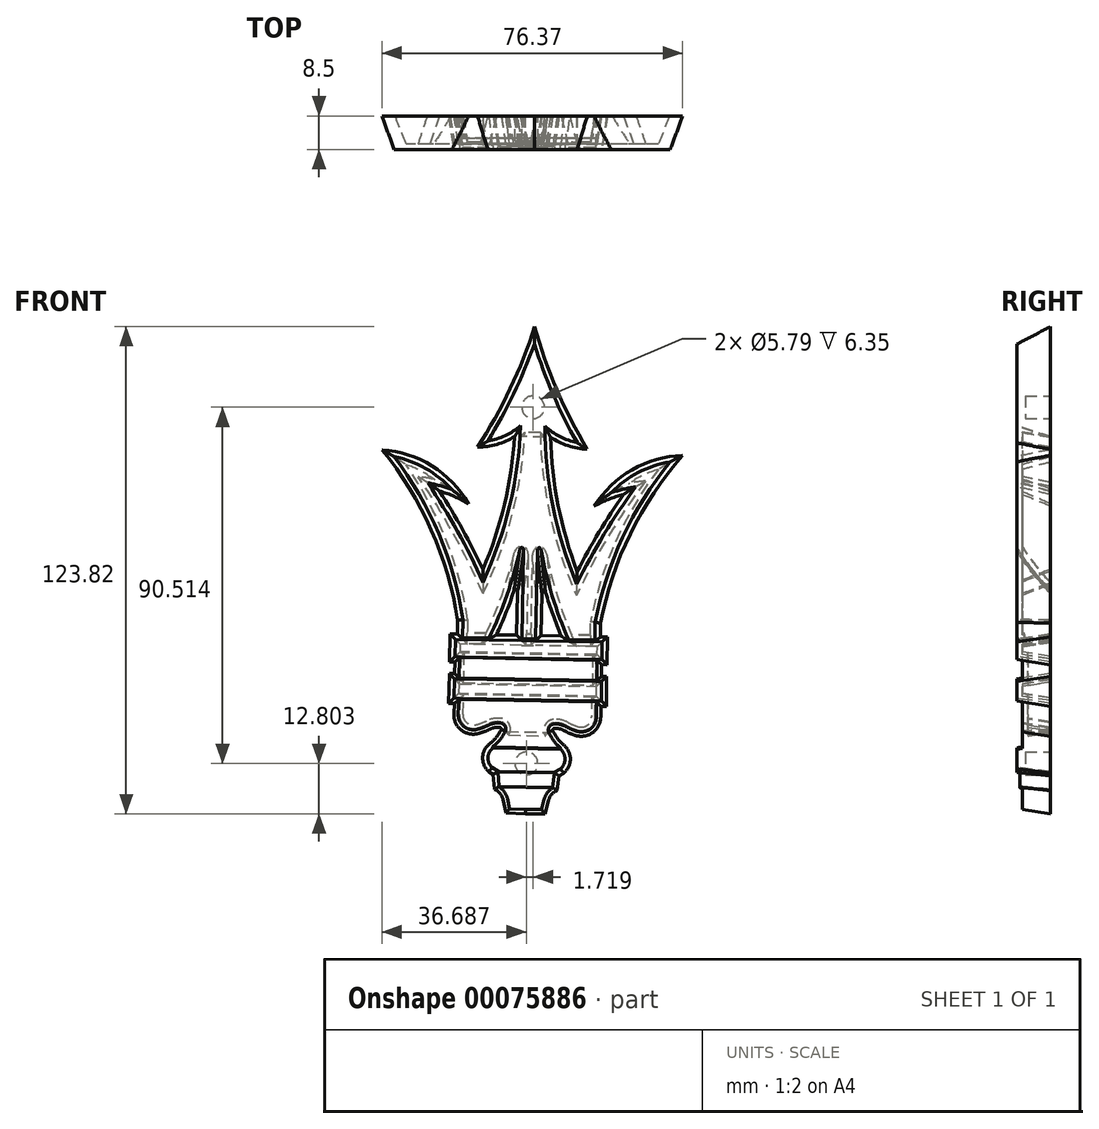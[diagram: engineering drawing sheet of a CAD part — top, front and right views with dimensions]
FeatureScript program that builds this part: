
annotation { "Feature Type Name" : "Feature", "Feature Type Description" : "" }
export const myFeature = defineFeature(function(context is Context, id is Id, definition is map)
    precondition{}
    {
        {
            var Q0;
            Q0=qCreatedBy(makeId("Front.planeOp"),FACE);
            var sketch = newSketch(context, id + "F0", { "sketchPlane" : qUnion([Q0])});
            skLineSegment(sketch, "E0", {"start": v(-26.98, -26.49) * mm, "end": v(-23.1, -26.49) * mm});
            skArc(sketch, "E1", {"start": v(-24.74, 91.51) * mm, "mid": v(-19.96, 78.7) * mm, "end": v(-13.84, 66.48) * mm});
            skArc(sketch, "E2", {"start": v(-22.03, 70.72) * mm, "mid": v(-18.24, 68.02) * mm, "end": v(-13.84, 66.48) * mm});
            skArc(sketch, "E3", {"start": v(-22.03, 70.72) * mm, "mid": v(-20, 50.24) * mm, "end": v(-14, 30.55) * mm});
            skArc(sketch, "E4", {"start": v(0.96, 55.26) * mm, "mid": v(-7.04, 43.22) * mm, "end": v(-14, 30.55) * mm});
            skArc(sketch, "E5", {"start": v(0.96, 55.26) * mm, "mid": v(-2.15, 54.66) * mm, "end": v(-5.19, 53.77) * mm});
            skArc(sketch, "E6", {"start": v(9.76, 61.58) * mm, "mid": v(1.64, 58.9) * mm, "end": v(-5.19, 53.77) * mm});
            skArc(sketch, "E7", {"start": v(9.76, 61.58) * mm, "mid": v(-2.3, 42.38) * mm, "end": v(-9.28, 20.8) * mm});
            skLineSegment(sketch, "E8", {"start": v(-9.28, 20.8) * mm, "end": v(-9.37, 15.85) * mm});
            skLineSegment(sketch, "E9", {"start": v(-9.37, 15.85) * mm, "end": v(-7.54, 15.82) * mm});
            skLineSegment(sketch, "E10", {"start": v(-7.54, 15.82) * mm, "end": v(-7.62, 11.41) * mm});
            skLineSegment(sketch, "E11", {"start": v(-7.62, 11.41) * mm, "end": v(-9.04, 11.44) * mm});
            skLineSegment(sketch, "E12", {"start": v(-9.04, 11.44) * mm, "end": v(-9.04, 5.77) * mm});
            skLineSegment(sketch, "E13", {"start": v(-9.04, 5.77) * mm, "end": v(-7.71, 5.77) * mm});
            skLineSegment(sketch, "E14", {"start": v(-7.71, 5.77) * mm, "end": v(-7.71, 0.87) * mm});
            skLineSegment(sketch, "E15", {"start": v(-7.71, 0.87) * mm, "end": v(-9.22, 0.87) * mm});
            skLineSegment(sketch, "E16", {"start": v(-9.22, 0.87) * mm, "end": v(-9.22, -3.16) * mm});
            skArc(sketch, "E17", {"start": v(-13.87, -6.61) * mm, "mid": v(-10.68, -6.06) * mm, "end": v(-9.22, -3.16) * mm});
            skArc(sketch, "E18", {"start": v(-16.67, -5.44) * mm, "mid": v(-15.3, -6.1) * mm, "end": v(-13.87, -6.61) * mm});
            skArc(sketch, "E19", {"start": v(-16.67, -5.44) * mm, "mid": v(-18.18, -4.88) * mm, "end": v(-19.78, -4.78) * mm});
            skArc(sketch, "E20", {"start": v(-19.78, -4.78) * mm, "mid": v(-21.12, -5.57) * mm, "end": v(-21.34, -7.1) * mm});
            skArc(sketch, "E21", {"start": v(-21.34, -7.1) * mm, "mid": v(-19.98, -9.44) * mm, "end": v(-18.11, -11.4) * mm});
            skArc(sketch, "E22", {"start": v(-18.11, -16.4) * mm, "mid": v(-16.94, -13.9) * mm, "end": v(-18.11, -11.4) * mm});
            skLineSegment(sketch, "E23", {"start": v(-18.11, -16.4) * mm, "end": v(-19.7, -17.36) * mm});
            skLineSegment(sketch, "E24", {"start": v(-19.7, -17.36) * mm, "end": v(-20.2, -21.02) * mm});
            skArc(sketch, "E25", {"start": v(-20.2, -21.02) * mm, "mid": v(-21.64, -22.32) * mm, "end": v(-22.48, -24.08) * mm});
            skLineSegment(sketch, "E26", {"start": v(-22.48, -24.08) * mm, "end": v(-23.1, -26.49) * mm});
            skLineSegment(sketch, "E27", {"start": v(-15.84, 15.97) * mm, "end": v(-24.42, 16.13) * mm});
            skLineSegment(sketch, "E28", {"start": v(-24.42, 16.13) * mm, "end": v(-23.86, 44.87) * mm});
            skArc(sketch, "E29", {"start": v(-23.86, 44.87) * mm, "mid": v(-20.95, 30.12) * mm, "end": v(-15.84, 15.97) * mm});
            skArc(sketch, "E30.MirrorCS", {"start": v(-24.74, 91.51) * mm, "mid": v(-30, 78.9) * mm, "end": v(-36.58, 66.91) * mm});
            skLineSegment(sketch, "E31.MirrorCS", {"start": v(-42.87, 21.44) * mm, "end": v(-42.97, 16.5) * mm});
            skLineSegment(sketch, "E32.MirrorCS", {"start": v(-42.97, 16.5) * mm, "end": v(-44.8, 16.53) * mm});
            skLineSegment(sketch, "E33.MirrorCS", {"start": v(-44.8, 16.53) * mm, "end": v(-44.89, 12.12) * mm});
            skLineSegment(sketch, "E34.MirrorCS", {"start": v(-44.89, 12.12) * mm, "end": v(-43.47, 12.1) * mm});
            skLineSegment(sketch, "E35.MirrorCS", {"start": v(-43.47, 12.1) * mm, "end": v(-43.68, 6.43) * mm});
            skLineSegment(sketch, "E36.MirrorCS", {"start": v(-43.68, 6.43) * mm, "end": v(-45.01, 6.48) * mm});
            skLineSegment(sketch, "E37.MirrorCS", {"start": v(-45.01, 6.48) * mm, "end": v(-45.2, 1.58) * mm});
            skLineSegment(sketch, "E38.MirrorCS", {"start": v(-45.2, 1.58) * mm, "end": v(-43.7, 1.52) * mm});
            skLineSegment(sketch, "E39.MirrorCS", {"start": v(-43.7, 1.52) * mm, "end": v(-43.85, -2.5) * mm});
            skArc(sketch, "E40.MirrorCS", {"start": v(-39.33, -6.13) * mm, "mid": v(-42.5, -5.45) * mm, "end": v(-43.85, -2.5) * mm});
            skArc(sketch, "E41.MirrorCS", {"start": v(-36.49, -5.06) * mm, "mid": v(-37.88, -5.67) * mm, "end": v(-39.33, -6.13) * mm});
            skArc(sketch, "E42.MirrorCS", {"start": v(-36.49, -5.06) * mm, "mid": v(-34.96, -4.56) * mm, "end": v(-33.35, -4.52) * mm});
            skArc(sketch, "E43.MirrorCS", {"start": v(-33.35, -4.52) * mm, "mid": v(-32.04, -5.36) * mm, "end": v(-31.88, -6.9) * mm});
            skArc(sketch, "E44.MirrorCS", {"start": v(-31.88, -6.9) * mm, "mid": v(-33.33, -9.18) * mm, "end": v(-35.27, -11.07) * mm});
            skArc(sketch, "E45.MirrorCS", {"start": v(-35.46, -16.06) * mm, "mid": v(-36.54, -13.52) * mm, "end": v(-35.27, -11.07) * mm});
            skLineSegment(sketch, "E46.MirrorCS", {"start": v(-35.46, -16.06) * mm, "end": v(-33.91, -17.1) * mm});
            skLineSegment(sketch, "E47.MirrorCS", {"start": v(-33.91, -17.1) * mm, "end": v(-33.56, -20.76) * mm});
            skArc(sketch, "E48.MirrorCS", {"start": v(-33.56, -20.76) * mm, "mid": v(-32.16, -22.12) * mm, "end": v(-31.39, -23.91) * mm});
            skLineSegment(sketch, "E49.MirrorCS", {"start": v(-31.39, -23.91) * mm, "end": v(-30.85, -26.34) * mm});
            skLineSegment(sketch, "E50.MirrorCS", {"start": v(-26.98, -26.49) * mm, "end": v(-30.85, -26.34) * mm});
            skLineSegment(sketch, "E51.MirrorCS", {"start": v(-36.5, 16.37) * mm, "end": v(-27.93, 16.2) * mm});
            skLineSegment(sketch, "E52.MirrorCS", {"start": v(-27.93, 16.2) * mm, "end": v(-27.4, 44.94) * mm});
            skArc(sketch, "E53.MirrorCS", {"start": v(-27.4, 44.94) * mm, "mid": v(-30.86, 30.3) * mm, "end": v(-36.5, 16.37) * mm});
            skArc(sketch, "E54.MirrorCS", {"start": v(-60.35, 62.9) * mm, "mid": v(-49.02, 43.27) * mm, "end": v(-42.87, 21.44) * mm});
            skArc(sketch, "E55.MirrorCS", {"start": v(-60.35, 62.9) * mm, "mid": v(-52.34, 59.93) * mm, "end": v(-45.71, 54.54) * mm});
            skArc(sketch, "E56.MirrorCS", {"start": v(-51.8, 56.26) * mm, "mid": v(-48.71, 55.55) * mm, "end": v(-45.71, 54.54) * mm});
            skArc(sketch, "E57.MirrorCS", {"start": v(-51.8, 56.26) * mm, "mid": v(-44.26, 43.93) * mm, "end": v(-37.8, 31) * mm});
            skArc(sketch, "E58.MirrorCS", {"start": v(-28.24, 70.83) * mm, "mid": v(-31.04, 50.45) * mm, "end": v(-37.8, 31) * mm});
            skArc(sketch, "E59.MirrorCS", {"start": v(-28.24, 70.83) * mm, "mid": v(-32.13, 68.28) * mm, "end": v(-36.58, 66.91) * mm});
            skSolve(sketch);
        }
        {
            var Q0;
            Q0=makeQuery(id+"F0.imprint","IMPRINT",FACE,{"disambiguationData":[TD([[makeQuery(id+"F0.imprint","IMPRINT",EDGE,{"derivedFrom":sQuery(id+"F0.wireOp",EDGE,"E0")}),1.0]])]});
            extrude(context, id + "F1", {"entities" : qUnion([Q0]), "oppositeDirection" : true, "depth" : 8.5 * mm, "hasDraft" : true, "draftAngle" : 9 * degree});
        }
        {
            var Q0;
            Q0=makeQuery(id+"F1.opExtrude","SWEPT_EDGE",EDGE,{"disambiguationData":[OSD([sQuery(id+"F0.wireOp",EDGE,"E52.MirrorCS"),sQuery(id+"F0.wireOp",EDGE,"E53.MirrorCS")])]});
            var Q1;
            Q1=makeQuery(id+"F1.opExtrude","SWEPT_EDGE",EDGE,{"disambiguationData":[OSD([sQuery(id+"F0.wireOp",EDGE,"E28"),sQuery(id+"F0.wireOp",EDGE,"E29")])]});
            fillet(context, id + "F2", {"entities" : qUnion([Q0, Q1]), "radius" : 0.5 * mm, "tangentPropagation" : true, "allowEdgeOverflow" : false});
        }
        {
            var Q0;
            Q0=makeQuery(id+"F1.opExtrude","CAP_FACE",FACE,{"disambiguationData":[OSD([sQuery(id+"F0.wireOp",EDGE,"E0"),sQuery(id+"F0.wireOp",EDGE,"E1"),sQuery(id+"F0.wireOp",EDGE,"E2"),sQuery(id+"F0.wireOp",EDGE,"E3"),sQuery(id+"F0.wireOp",EDGE,"E4"),sQuery(id+"F0.wireOp",EDGE,"E5"),sQuery(id+"F0.wireOp",EDGE,"E6"),sQuery(id+"F0.wireOp",EDGE,"E7"),sQuery(id+"F0.wireOp",EDGE,"E8"),sQuery(id+"F0.wireOp",EDGE,"E9"),sQuery(id+"F0.wireOp",EDGE,"E10"),sQuery(id+"F0.wireOp",EDGE,"E11"),sQuery(id+"F0.wireOp",EDGE,"E12"),sQuery(id+"F0.wireOp",EDGE,"E13"),sQuery(id+"F0.wireOp",EDGE,"E14"),sQuery(id+"F0.wireOp",EDGE,"E15"),sQuery(id+"F0.wireOp",EDGE,"E16"),sQuery(id+"F0.wireOp",EDGE,"E17"),sQuery(id+"F0.wireOp",EDGE,"E18"),sQuery(id+"F0.wireOp",EDGE,"E19"),sQuery(id+"F0.wireOp",EDGE,"E20"),sQuery(id+"F0.wireOp",EDGE,"E21"),sQuery(id+"F0.wireOp",EDGE,"E22"),sQuery(id+"F0.wireOp",EDGE,"E23"),sQuery(id+"F0.wireOp",EDGE,"E24"),sQuery(id+"F0.wireOp",EDGE,"E25"),sQuery(id+"F0.wireOp",EDGE,"E26"),sQuery(id+"F0.wireOp",EDGE,"E27"),sQuery(id+"F0.wireOp",EDGE,"E28"),sQuery(id+"F0.wireOp",EDGE,"E29"),sQuery(id+"F0.wireOp",EDGE,"E30.MirrorCS"),sQuery(id+"F0.wireOp",EDGE,"E31.MirrorCS"),sQuery(id+"F0.wireOp",EDGE,"E32.MirrorCS"),sQuery(id+"F0.wireOp",EDGE,"E33.MirrorCS"),sQuery(id+"F0.wireOp",EDGE,"E34.MirrorCS"),sQuery(id+"F0.wireOp",EDGE,"E35.MirrorCS"),sQuery(id+"F0.wireOp",EDGE,"E36.MirrorCS"),sQuery(id+"F0.wireOp",EDGE,"E37.MirrorCS"),sQuery(id+"F0.wireOp",EDGE,"E38.MirrorCS"),sQuery(id+"F0.wireOp",EDGE,"E39.MirrorCS"),sQuery(id+"F0.wireOp",EDGE,"E40.MirrorCS"),sQuery(id+"F0.wireOp",EDGE,"E41.MirrorCS"),sQuery(id+"F0.wireOp",EDGE,"E42.MirrorCS"),sQuery(id+"F0.wireOp",EDGE,"E43.MirrorCS"),sQuery(id+"F0.wireOp",EDGE,"E44.MirrorCS"),sQuery(id+"F0.wireOp",EDGE,"E45.MirrorCS"),sQuery(id+"F0.wireOp",EDGE,"E46.MirrorCS"),sQuery(id+"F0.wireOp",EDGE,"E47.MirrorCS"),sQuery(id+"F0.wireOp",EDGE,"E48.MirrorCS"),sQuery(id+"F0.wireOp",EDGE,"E49.MirrorCS"),sQuery(id+"F0.wireOp",EDGE,"E50.MirrorCS"),sQuery(id+"F0.wireOp",EDGE,"E51.MirrorCS"),sQuery(id+"F0.wireOp",EDGE,"E52.MirrorCS"),sQuery(id+"F0.wireOp",EDGE,"E53.MirrorCS"),sQuery(id+"F0.wireOp",EDGE,"E54.MirrorCS"),sQuery(id+"F0.wireOp",EDGE,"E55.MirrorCS"),sQuery(id+"F0.wireOp",EDGE,"E56.MirrorCS"),sQuery(id+"F0.wireOp",EDGE,"E57.MirrorCS"),sQuery(id+"F0.wireOp",EDGE,"E58.MirrorCS"),sQuery(id+"F0.wireOp",EDGE,"E59.MirrorCS")])],"isStart":true});
            var sketch = newSketch(context, id + "F3", { "sketchPlane" : qUnion([Q0])});
            skLineSegment(sketch, "E60", {"start": v(-43.47, 12.1) * mm, "end": v(-9.04, 11.44) * mm});
            skLineSegment(sketch, "E61", {"start": v(-9.04, 5.77) * mm, "end": v(-43.68, 6.43) * mm});
            skLineSegment(sketch, "E62", {"start": v(-43.7, 1.52) * mm, "end": v(-9.22, 0.87) * mm});
            skLineSegment(sketch, "E63", {"start": v(-9.22, 0.87) * mm, "end": v(-3.24, 0.87) * mm});
            skLineSegment(sketch, "E64", {"start": v(-3.24, 0.87) * mm, "end": v(-9.14, -11.57) * mm});
            skLineSegment(sketch, "E65", {"start": v(-9.14, -11.57) * mm, "end": v(-18.11, -11.4) * mm});
            skLineSegment(sketch, "E66", {"start": v(-18.11, -11.4) * mm, "end": v(-35.27, -11.07) * mm});
            skLineSegment(sketch, "E67", {"start": v(-35.27, -11.07) * mm, "end": v(-45.82, -10.87) * mm});
            skLineSegment(sketch, "E68", {"start": v(-45.82, -10.87) * mm, "end": v(-49.07, 1.73) * mm});
            skLineSegment(sketch, "E69", {"start": v(-49.07, 1.73) * mm, "end": v(-43.7, 1.52) * mm});
            skLineSegment(sketch, "E70", {"start": v(-33.56, -20.76) * mm, "end": v(-20.2, -21.02) * mm});
            skLineSegment(sketch, "E71", {"start": v(-20.2, -21.02) * mm, "end": v(-18, -22.48) * mm});
            skLineSegment(sketch, "E72", {"start": v(-18, -22.48) * mm, "end": v(-21.3, -29.33) * mm});
            skLineSegment(sketch, "E73", {"start": v(-21.3, -29.33) * mm, "end": v(-32.58, -28.86) * mm});
            skLineSegment(sketch, "E74", {"start": v(-32.58, -28.86) * mm, "end": v(-35.83, -22.18) * mm});
            skLineSegment(sketch, "E75", {"start": v(-35.83, -22.18) * mm, "end": v(-33.56, -20.76) * mm});
            skLineSegment(sketch, "E76", {"start": v(-43.47, 12.1) * mm, "end": v(-48.18, 12.19) * mm});
            skLineSegment(sketch, "E77", {"start": v(-48.18, 12.19) * mm, "end": v(-48.29, 6.6) * mm});
            skLineSegment(sketch, "E78", {"start": v(-48.29, 6.6) * mm, "end": v(-43.68, 6.43) * mm});
            skLineSegment(sketch, "E79", {"start": v(-9.04, 11.44) * mm, "end": v(-3.44, 11.34) * mm});
            skLineSegment(sketch, "E80", {"start": v(-3.44, 11.34) * mm, "end": v(-3.1, 5.77) * mm});
            skLineSegment(sketch, "E81", {"start": v(-3.1, 5.77) * mm, "end": v(-9.04, 5.77) * mm});
            skSolve(sketch);
        }
        {
            var Q0;
            {var subQ2=sQuery(id+"F3.wireOp",EDGE,"E77");Q0=makeQuery(id+"F3.imprint","IMPRINT",FACE,{"disambiguationData":[TD([[makeQuery(id+"F3.imprint","IMPRINT",EDGE,{"derivedFrom":subQ2}),1.0]])]});}
            var Q1;
            Q1=makeQuery(id+"F3.imprint","IMPRINT",FACE,{"disambiguationData":[TD([[makeQuery(id+"F3.imprint","IMPRINT",EDGE,{"derivedFrom":sQuery(id+"F3.wireOp",EDGE,"E60")}),-1.0]])]});
            var Q2;
            {var subQ0=sQuery(id+"F3.wireOp",EDGE,"E80");Q2=makeQuery(id+"F3.imprint","IMPRINT",FACE,{"disambiguationData":[TD([[makeQuery(id+"F3.imprint","IMPRINT",EDGE,{"derivedFrom":subQ0}),-1.0]])]});}
            var Q3;
            Q3=makeQuery(id+"F3.imprint","IMPRINT",FACE,{"disambiguationData":[TD([[makeQuery(id+"F3.imprint","IMPRINT",EDGE,{"derivedFrom":sQuery(id+"F3.wireOp",EDGE,"E67")}),-1.0]])]});
            var Q4;
            Q4=makeQuery(id+"F3.imprint","IMPRINT",FACE,{"disambiguationData":[TD([[makeQuery(id+"F3.imprint","IMPRINT",EDGE,{"derivedFrom":sQuery(id+"F3.wireOp",EDGE,"E62")}),-1.0]])]});
            var Q5;
            {var subQ3=sQuery(id+"F3.wireOp",EDGE,"E64");Q5=makeQuery(id+"F3.imprint","IMPRINT",FACE,{"disambiguationData":[TD([[makeQuery(id+"F3.imprint","IMPRINT",EDGE,{"derivedFrom":subQ3}),-1.0]])]});}
            var Q6;
            Q6=makeQuery(id+"F3.imprint","IMPRINT",FACE,{"disambiguationData":[TD([[makeQuery(id+"F3.imprint","IMPRINT",EDGE,{"derivedFrom":sQuery(id+"F3.wireOp",EDGE,"E70")}),-1.0]])]});
            var Q7;
            Q7=makeQuery(id+"F3.imprint","IMPRINT",FACE,{"disambiguationData":[TD([[makeQuery(id+"F3.imprint","IMPRINT",EDGE,{"derivedFrom":sQuery(id+"F3.wireOp",EDGE,"E71")}),-1.0]])]});
            extrude(context, id + "F4", {"entities" : qUnion([Q0, Q1, Q2, Q3, Q4, Q5, Q6, Q7]), "operationType" : NewBodyOperationType.REMOVE, "oppositeDirection" : true, "depth" : 1.5 * mm, "hasDraft" : true, "draftAngle" : 9 * degree, "draftPullDirection" : true});
        }
        {
            var Q0;
            {var subQ0=sQuery(id+"F0.wireOp",EDGE,"E48.MirrorCS");var subQ1=sQuery(id+"F0.wireOp",EDGE,"E24");var subQ2=sQuery(id+"F0.wireOp",EDGE,"E47.MirrorCS");var subQ3=sQuery(id+"F0.wireOp",EDGE,"E23");var subQ4=sQuery(id+"F0.wireOp",EDGE,"E46.MirrorCS");var subQ5=sQuery(id+"F0.wireOp",EDGE,"E25");var subQ6=sQuery(id+"F0.wireOp",EDGE,"E22");var subQ7=sQuery(id+"F0.wireOp",EDGE,"E21");var subQ8=sQuery(id+"F0.wireOp",EDGE,"E44.MirrorCS");var subQ9=sQuery(id+"F0.wireOp",EDGE,"E45.MirrorCS");Q0=makeQuery(id+"F4.boolean.opBoolean","SPLIT",FACE,{"disambiguationData":[TD([makeQuery(id+"F1.opExtrude","SWEPT_FACE",FACE,{"disambiguationData":[OSD([subQ7])]})])],"derivedFrom":makeQuery(id+"F1.opExtrude","CAP_FACE",FACE,{"disambiguationData":[OSD([sQuery(id+"F0.wireOp",EDGE,"E0"),sQuery(id+"F0.wireOp",EDGE,"E1"),sQuery(id+"F0.wireOp",EDGE,"E2"),sQuery(id+"F0.wireOp",EDGE,"E3"),sQuery(id+"F0.wireOp",EDGE,"E4"),sQuery(id+"F0.wireOp",EDGE,"E5"),sQuery(id+"F0.wireOp",EDGE,"E6"),sQuery(id+"F0.wireOp",EDGE,"E7"),sQuery(id+"F0.wireOp",EDGE,"E8"),sQuery(id+"F0.wireOp",EDGE,"E9"),sQuery(id+"F0.wireOp",EDGE,"E10"),sQuery(id+"F0.wireOp",EDGE,"E11"),sQuery(id+"F0.wireOp",EDGE,"E12"),sQuery(id+"F0.wireOp",EDGE,"E13"),sQuery(id+"F0.wireOp",EDGE,"E14"),sQuery(id+"F0.wireOp",EDGE,"E15"),sQuery(id+"F0.wireOp",EDGE,"E16"),sQuery(id+"F0.wireOp",EDGE,"E17"),sQuery(id+"F0.wireOp",EDGE,"E18"),sQuery(id+"F0.wireOp",EDGE,"E19"),sQuery(id+"F0.wireOp",EDGE,"E20"),subQ7,subQ6,subQ3,subQ1,subQ5,sQuery(id+"F0.wireOp",EDGE,"E26"),sQuery(id+"F0.wireOp",EDGE,"E27"),sQuery(id+"F0.wireOp",EDGE,"E28"),sQuery(id+"F0.wireOp",EDGE,"E29"),sQuery(id+"F0.wireOp",EDGE,"E30.MirrorCS"),sQuery(id+"F0.wireOp",EDGE,"E31.MirrorCS"),sQuery(id+"F0.wireOp",EDGE,"E32.MirrorCS"),sQuery(id+"F0.wireOp",EDGE,"E33.MirrorCS"),sQuery(id+"F0.wireOp",EDGE,"E34.MirrorCS"),sQuery(id+"F0.wireOp",EDGE,"E35.MirrorCS"),sQuery(id+"F0.wireOp",EDGE,"E36.MirrorCS"),sQuery(id+"F0.wireOp",EDGE,"E37.MirrorCS"),sQuery(id+"F0.wireOp",EDGE,"E38.MirrorCS"),sQuery(id+"F0.wireOp",EDGE,"E39.MirrorCS"),sQuery(id+"F0.wireOp",EDGE,"E40.MirrorCS"),sQuery(id+"F0.wireOp",EDGE,"E41.MirrorCS"),sQuery(id+"F0.wireOp",EDGE,"E42.MirrorCS"),sQuery(id+"F0.wireOp",EDGE,"E43.MirrorCS"),subQ8,subQ9,subQ4,subQ2,subQ0,sQuery(id+"F0.wireOp",EDGE,"E49.MirrorCS"),sQuery(id+"F0.wireOp",EDGE,"E50.MirrorCS"),sQuery(id+"F0.wireOp",EDGE,"E51.MirrorCS"),sQuery(id+"F0.wireOp",EDGE,"E52.MirrorCS"),sQuery(id+"F0.wireOp",EDGE,"E53.MirrorCS"),sQuery(id+"F0.wireOp",EDGE,"E54.MirrorCS"),sQuery(id+"F0.wireOp",EDGE,"E55.MirrorCS"),sQuery(id+"F0.wireOp",EDGE,"E56.MirrorCS"),sQuery(id+"F0.wireOp",EDGE,"E57.MirrorCS"),sQuery(id+"F0.wireOp",EDGE,"E58.MirrorCS"),sQuery(id+"F0.wireOp",EDGE,"E59.MirrorCS")])],"isStart":true})});}
            var sketch = newSketch(context, id + "F5", { "sketchPlane" : qUnion([Q0])});
            skLineSegment(sketch, "E82", {"start": v(-33.91, -17.1) * mm, "end": v(-19.7, -17.36) * mm});
            skLineSegment(sketch, "E83", {"start": v(-19.7, -17.36) * mm, "end": v(-16.05, -17.43) * mm});
            skLineSegment(sketch, "E84", {"start": v(-16.05, -17.43) * mm, "end": v(-18.1, -23.56) * mm});
            skLineSegment(sketch, "E85", {"start": v(-18.1, -23.56) * mm, "end": v(-35.42, -23.56) * mm});
            skLineSegment(sketch, "E86", {"start": v(-35.42, -23.56) * mm, "end": v(-36.7, -17.04) * mm});
            skLineSegment(sketch, "E87", {"start": v(-36.7, -17.04) * mm, "end": v(-33.91, -17.1) * mm});
            skSolve(sketch);
        }
        {
            var Q0;
            Q0 = qSketchRegion(id + "F5", true);
            extrude(context, id + "F6", {"entities" : qUnion([Q0]), "operationType" : NewBodyOperationType.REMOVE, "oppositeDirection" : true, "depth" : 0.75 * mm, "hasDraft" : true, "draftAngle" : 9 * degree, "draftPullDirection" : true});
        }
        {
            var Q0;
            {var subQ0=sQuery(id+"F0.wireOp",EDGE,"E53.MirrorCS");var subQ1=sQuery(id+"F0.wireOp",EDGE,"E4");var subQ2=sQuery(id+"F0.wireOp",EDGE,"E31.MirrorCS");var subQ3=sQuery(id+"F0.wireOp",EDGE,"E33.MirrorCS");var subQ4=sQuery(id+"F0.wireOp",EDGE,"E30.MirrorCS");var subQ5=sQuery(id+"F0.wireOp",EDGE,"E32.MirrorCS");var subQ6=sQuery(id+"F0.wireOp",EDGE,"E51.MirrorCS");var subQ7=sQuery(id+"F0.wireOp",EDGE,"E2");var subQ8=sQuery(id+"F0.wireOp",EDGE,"E59.MirrorCS");var subQ9=sQuery(id+"F0.wireOp",EDGE,"E34.MirrorCS");var subQ10=sQuery(id+"F0.wireOp",EDGE,"E27");var subQ11=sQuery(id+"F0.wireOp",EDGE,"E11");var subQ12=sQuery(id+"F0.wireOp",EDGE,"E58.MirrorCS");var subQ13=sQuery(id+"F0.wireOp",EDGE,"E3");var subQ14=sQuery(id+"F0.wireOp",EDGE,"E52.MirrorCS");var subQ15=sQuery(id+"F0.wireOp",EDGE,"E10");var subQ16=sQuery(id+"F0.wireOp",EDGE,"E28");var subQ17=sQuery(id+"F0.wireOp",EDGE,"E1");var subQ18=sQuery(id+"F0.wireOp",EDGE,"E8");var subQ19=sQuery(id+"F0.wireOp",EDGE,"E57.MirrorCS");var subQ20=sQuery(id+"F0.wireOp",EDGE,"E29");var subQ21=sQuery(id+"F0.wireOp",EDGE,"E5");var subQ22=sQuery(id+"F0.wireOp",EDGE,"E6");var subQ23=sQuery(id+"F0.wireOp",EDGE,"E55.MirrorCS");var subQ24=sQuery(id+"F0.wireOp",EDGE,"E7");var subQ25=sQuery(id+"F0.wireOp",EDGE,"E54.MirrorCS");var subQ26=sQuery(id+"F0.wireOp",EDGE,"E56.MirrorCS");var subQ27=sQuery(id+"F0.wireOp",EDGE,"E9");Q0=makeQuery(id+"F4.boolean.opBoolean","SPLIT",FACE,{"disambiguationData":[TD([makeQuery(id+"F1.opExtrude","SWEPT_FACE",FACE,{"disambiguationData":[OSD([subQ17])]})])],"derivedFrom":makeQuery(id+"F1.opExtrude","CAP_FACE",FACE,{"disambiguationData":[OSD([sQuery(id+"F0.wireOp",EDGE,"E0"),subQ17,subQ7,subQ13,subQ1,subQ21,subQ22,subQ24,subQ18,subQ27,subQ15,subQ11,sQuery(id+"F0.wireOp",EDGE,"E12"),sQuery(id+"F0.wireOp",EDGE,"E13"),sQuery(id+"F0.wireOp",EDGE,"E14"),sQuery(id+"F0.wireOp",EDGE,"E15"),sQuery(id+"F0.wireOp",EDGE,"E16"),sQuery(id+"F0.wireOp",EDGE,"E17"),sQuery(id+"F0.wireOp",EDGE,"E18"),sQuery(id+"F0.wireOp",EDGE,"E19"),sQuery(id+"F0.wireOp",EDGE,"E20"),sQuery(id+"F0.wireOp",EDGE,"E21"),sQuery(id+"F0.wireOp",EDGE,"E22"),sQuery(id+"F0.wireOp",EDGE,"E23"),sQuery(id+"F0.wireOp",EDGE,"E24"),sQuery(id+"F0.wireOp",EDGE,"E25"),sQuery(id+"F0.wireOp",EDGE,"E26"),subQ10,subQ16,subQ20,subQ4,subQ2,subQ5,subQ3,subQ9,sQuery(id+"F0.wireOp",EDGE,"E35.MirrorCS"),sQuery(id+"F0.wireOp",EDGE,"E36.MirrorCS"),sQuery(id+"F0.wireOp",EDGE,"E37.MirrorCS"),sQuery(id+"F0.wireOp",EDGE,"E38.MirrorCS"),sQuery(id+"F0.wireOp",EDGE,"E39.MirrorCS"),sQuery(id+"F0.wireOp",EDGE,"E40.MirrorCS"),sQuery(id+"F0.wireOp",EDGE,"E41.MirrorCS"),sQuery(id+"F0.wireOp",EDGE,"E42.MirrorCS"),sQuery(id+"F0.wireOp",EDGE,"E43.MirrorCS"),sQuery(id+"F0.wireOp",EDGE,"E44.MirrorCS"),sQuery(id+"F0.wireOp",EDGE,"E45.MirrorCS"),sQuery(id+"F0.wireOp",EDGE,"E46.MirrorCS"),sQuery(id+"F0.wireOp",EDGE,"E47.MirrorCS"),sQuery(id+"F0.wireOp",EDGE,"E48.MirrorCS"),sQuery(id+"F0.wireOp",EDGE,"E49.MirrorCS"),sQuery(id+"F0.wireOp",EDGE,"E50.MirrorCS"),subQ6,subQ14,subQ0,subQ25,subQ23,subQ26,subQ19,subQ12,subQ8])],"isStart":true})});}
            var sketch = newSketch(context, id + "F7", { "sketchPlane" : qUnion([Q0])});
            skLineSegment(sketch, "E88", {"start": v(-42.97, 16.5) * mm, "end": v(-36.5, 16.37) * mm});
            skLineSegment(sketch, "E89", {"start": v(-36.5, 16.37) * mm, "end": v(-27.93, 16.2) * mm});
            skLineSegment(sketch, "E90", {"start": v(-27.93, 16.2) * mm, "end": v(-24.42, 16.13) * mm});
            skLineSegment(sketch, "E91", {"start": v(-24.42, 16.13) * mm, "end": v(-15.84, 15.97) * mm});
            skLineSegment(sketch, "E92", {"start": v(-15.84, 15.97) * mm, "end": v(-9.37, 15.85) * mm});
            skLineSegment(sketch, "E93", {"start": v(-9.37, 15.85) * mm, "end": v(-7.54, 15.82) * mm});
            skLineSegment(sketch, "E94", {"start": v(-42.97, 16.5) * mm, "end": v(-44.8, 16.53) * mm});
            skLineSegment(sketch, "E95.0", {"start": v(-42.96, 17) * mm, "end": v(-44.8, 17.03) * mm});
            skLineSegment(sketch, "E95.1", {"start": v(-42.96, 17) * mm, "end": v(-36.5, 16.87) * mm});
            skLineSegment(sketch, "E95.2", {"start": v(-36.5, 16.87) * mm, "end": v(-27.92, 16.7) * mm});
            skLineSegment(sketch, "E95.3", {"start": v(-9.36, 16.35) * mm, "end": v(-7.53, 16.32) * mm});
            skLineSegment(sketch, "E95.4", {"start": v(-15.83, 16.47) * mm, "end": v(-9.36, 16.35) * mm});
            skLineSegment(sketch, "E95.5", {"start": v(-24.4, 16.63) * mm, "end": v(-15.83, 16.47) * mm});
            skLineSegment(sketch, "E95.6", {"start": v(-27.92, 16.7) * mm, "end": v(-24.4, 16.63) * mm});
            skLineSegment(sketch, "E96", {"start": v(-44.8, 16.53) * mm, "end": v(-44.8, 17.03) * mm});
            skLineSegment(sketch, "E97", {"start": v(-7.54, 15.82) * mm, "end": v(-7.53, 16.32) * mm});
            skSolve(sketch);
        }
        {
            var Q0;
            {var subQ0=sQuery(id+"F7.wireOp",EDGE,"E94");Q0=makeQuery(id+"F7.imprint","IMPRINT",FACE,{"disambiguationData":[TD([[makeQuery(id+"F7.imprint","IMPRINT",EDGE,{"derivedFrom":subQ0}),-1.0]])]});}
            var Q1;
            {var subQ0=sQuery(id+"F7.wireOp",EDGE,"E88");Q1=makeQuery(id+"F7.imprint","IMPRINT",FACE,{"disambiguationData":[TD([[makeQuery(id+"F7.imprint","IMPRINT",EDGE,{"derivedFrom":subQ0}),1.0]])]});}
            var Q2;
            {var subQ0=sQuery(id+"F7.wireOp",EDGE,"E89");Q2=makeQuery(id+"F7.imprint","IMPRINT",FACE,{"disambiguationData":[TD([[makeQuery(id+"F7.imprint","IMPRINT",EDGE,{"derivedFrom":subQ0}),1.0]])]});}
            var Q3;
            {var subQ1=sQuery(id+"F7.wireOp",EDGE,"E90");Q3=makeQuery(id+"F7.imprint","IMPRINT",FACE,{"disambiguationData":[TD([[makeQuery(id+"F7.imprint","IMPRINT",EDGE,{"derivedFrom":subQ1}),1.0]])]});}
            var Q4;
            {var subQ0=sQuery(id+"F7.wireOp",EDGE,"E91");Q4=makeQuery(id+"F7.imprint","IMPRINT",FACE,{"disambiguationData":[TD([[makeQuery(id+"F7.imprint","IMPRINT",EDGE,{"derivedFrom":subQ0}),-1.0]])]});}
            var Q5;
            {var subQ4=sQuery(id+"F7.wireOp",EDGE,"E92");Q5=makeQuery(id+"F7.imprint","IMPRINT",FACE,{"disambiguationData":[TD([[makeQuery(id+"F7.imprint","IMPRINT",EDGE,{"derivedFrom":subQ4}),1.0]])]});}
            var Q6;
            {var subQ0=sQuery(id+"F7.wireOp",EDGE,"E93");Q6=makeQuery(id+"F7.imprint","IMPRINT",FACE,{"disambiguationData":[TD([[makeQuery(id+"F7.imprint","IMPRINT",EDGE,{"derivedFrom":subQ0}),1.0]])]});}
            extrude(context, id + "F8", {"entities" : qUnion([Q0, Q1, Q2, Q3, Q4, Q5, Q6]), "operationType" : NewBodyOperationType.REMOVE, "oppositeDirection" : true, "depth" : 0.5 * mm, "hasDraft" : true, "draftAngle" : 9 * degree, "draftPullDirection" : true});
        }
        {
            var Q0;
            Q0=makeQuery(id+"F1.opExtrude","CAP_FACE",FACE,{"disambiguationData":[OSD([sQuery(id+"F0.wireOp",EDGE,"E0"),sQuery(id+"F0.wireOp",EDGE,"E1"),sQuery(id+"F0.wireOp",EDGE,"E2"),sQuery(id+"F0.wireOp",EDGE,"E3"),sQuery(id+"F0.wireOp",EDGE,"E4"),sQuery(id+"F0.wireOp",EDGE,"E5"),sQuery(id+"F0.wireOp",EDGE,"E6"),sQuery(id+"F0.wireOp",EDGE,"E7"),sQuery(id+"F0.wireOp",EDGE,"E8"),sQuery(id+"F0.wireOp",EDGE,"E9"),sQuery(id+"F0.wireOp",EDGE,"E10"),sQuery(id+"F0.wireOp",EDGE,"E11"),sQuery(id+"F0.wireOp",EDGE,"E12"),sQuery(id+"F0.wireOp",EDGE,"E13"),sQuery(id+"F0.wireOp",EDGE,"E14"),sQuery(id+"F0.wireOp",EDGE,"E15"),sQuery(id+"F0.wireOp",EDGE,"E16"),sQuery(id+"F0.wireOp",EDGE,"E17"),sQuery(id+"F0.wireOp",EDGE,"E18"),sQuery(id+"F0.wireOp",EDGE,"E19"),sQuery(id+"F0.wireOp",EDGE,"E20"),sQuery(id+"F0.wireOp",EDGE,"E21"),sQuery(id+"F0.wireOp",EDGE,"E22"),sQuery(id+"F0.wireOp",EDGE,"E23"),sQuery(id+"F0.wireOp",EDGE,"E24"),sQuery(id+"F0.wireOp",EDGE,"E25"),sQuery(id+"F0.wireOp",EDGE,"E26"),sQuery(id+"F0.wireOp",EDGE,"E27"),sQuery(id+"F0.wireOp",EDGE,"E28"),sQuery(id+"F0.wireOp",EDGE,"E29"),sQuery(id+"F0.wireOp",EDGE,"E30.MirrorCS"),sQuery(id+"F0.wireOp",EDGE,"E31.MirrorCS"),sQuery(id+"F0.wireOp",EDGE,"E32.MirrorCS"),sQuery(id+"F0.wireOp",EDGE,"E33.MirrorCS"),sQuery(id+"F0.wireOp",EDGE,"E34.MirrorCS"),sQuery(id+"F0.wireOp",EDGE,"E35.MirrorCS"),sQuery(id+"F0.wireOp",EDGE,"E36.MirrorCS"),sQuery(id+"F0.wireOp",EDGE,"E37.MirrorCS"),sQuery(id+"F0.wireOp",EDGE,"E38.MirrorCS"),sQuery(id+"F0.wireOp",EDGE,"E39.MirrorCS"),sQuery(id+"F0.wireOp",EDGE,"E40.MirrorCS"),sQuery(id+"F0.wireOp",EDGE,"E41.MirrorCS"),sQuery(id+"F0.wireOp",EDGE,"E42.MirrorCS"),sQuery(id+"F0.wireOp",EDGE,"E43.MirrorCS"),sQuery(id+"F0.wireOp",EDGE,"E44.MirrorCS"),sQuery(id+"F0.wireOp",EDGE,"E45.MirrorCS"),sQuery(id+"F0.wireOp",EDGE,"E46.MirrorCS"),sQuery(id+"F0.wireOp",EDGE,"E47.MirrorCS"),sQuery(id+"F0.wireOp",EDGE,"E48.MirrorCS"),sQuery(id+"F0.wireOp",EDGE,"E49.MirrorCS"),sQuery(id+"F0.wireOp",EDGE,"E50.MirrorCS"),sQuery(id+"F0.wireOp",EDGE,"E51.MirrorCS"),sQuery(id+"F0.wireOp",EDGE,"E52.MirrorCS"),sQuery(id+"F0.wireOp",EDGE,"E53.MirrorCS"),sQuery(id+"F0.wireOp",EDGE,"E54.MirrorCS"),sQuery(id+"F0.wireOp",EDGE,"E55.MirrorCS"),sQuery(id+"F0.wireOp",EDGE,"E56.MirrorCS"),sQuery(id+"F0.wireOp",EDGE,"E57.MirrorCS"),sQuery(id+"F0.wireOp",EDGE,"E58.MirrorCS"),sQuery(id+"F0.wireOp",EDGE,"E59.MirrorCS")])],"isStart":false});
            shell(context, id + "F9", {"entities" : qUnion([Q0]), "thickness" : 1.4 * mm});
        }
        {
            var Q0;
            {var subQ0=sQuery(id+"F0.wireOp",EDGE,"E59.MirrorCS");var subQ1=sQuery(id+"F0.wireOp",EDGE,"E58.MirrorCS");var subQ2=sQuery(id+"F0.wireOp",EDGE,"E57.MirrorCS");var subQ3=sQuery(id+"F0.wireOp",EDGE,"E56.MirrorCS");var subQ4=sQuery(id+"F0.wireOp",EDGE,"E55.MirrorCS");var subQ5=sQuery(id+"F0.wireOp",EDGE,"E54.MirrorCS");var subQ6=sQuery(id+"F0.wireOp",EDGE,"E53.MirrorCS");var subQ7=sQuery(id+"F0.wireOp",EDGE,"E52.MirrorCS");var subQ8=sQuery(id+"F0.wireOp",EDGE,"E51.MirrorCS");var subQ9=sQuery(id+"F0.wireOp",EDGE,"E50.MirrorCS");var subQ10=sQuery(id+"F0.wireOp",EDGE,"E49.MirrorCS");var subQ11=sQuery(id+"F0.wireOp",EDGE,"E48.MirrorCS");var subQ12=sQuery(id+"F0.wireOp",EDGE,"E47.MirrorCS");var subQ13=sQuery(id+"F0.wireOp",EDGE,"E46.MirrorCS");var subQ14=sQuery(id+"F0.wireOp",EDGE,"E45.MirrorCS");var subQ15=sQuery(id+"F0.wireOp",EDGE,"E44.MirrorCS");var subQ16=sQuery(id+"F0.wireOp",EDGE,"E43.MirrorCS");var subQ17=sQuery(id+"F0.wireOp",EDGE,"E42.MirrorCS");var subQ18=sQuery(id+"F0.wireOp",EDGE,"E41.MirrorCS");var subQ19=sQuery(id+"F0.wireOp",EDGE,"E40.MirrorCS");var subQ20=sQuery(id+"F0.wireOp",EDGE,"E39.MirrorCS");var subQ21=sQuery(id+"F0.wireOp",EDGE,"E38.MirrorCS");var subQ22=sQuery(id+"F0.wireOp",EDGE,"E37.MirrorCS");var subQ23=sQuery(id+"F0.wireOp",EDGE,"E36.MirrorCS");var subQ24=sQuery(id+"F0.wireOp",EDGE,"E35.MirrorCS");var subQ25=sQuery(id+"F0.wireOp",EDGE,"E34.MirrorCS");var subQ26=sQuery(id+"F0.wireOp",EDGE,"E33.MirrorCS");var subQ27=sQuery(id+"F0.wireOp",EDGE,"E32.MirrorCS");var subQ28=sQuery(id+"F0.wireOp",EDGE,"E31.MirrorCS");var subQ29=sQuery(id+"F0.wireOp",EDGE,"E30.MirrorCS");var subQ30=sQuery(id+"F0.wireOp",EDGE,"E29");var subQ31=sQuery(id+"F0.wireOp",EDGE,"E28");var subQ32=sQuery(id+"F0.wireOp",EDGE,"E27");var subQ33=sQuery(id+"F0.wireOp",EDGE,"E26");var subQ34=sQuery(id+"F0.wireOp",EDGE,"E25");var subQ35=sQuery(id+"F0.wireOp",EDGE,"E24");var subQ36=sQuery(id+"F0.wireOp",EDGE,"E23");var subQ37=sQuery(id+"F0.wireOp",EDGE,"E22");var subQ38=sQuery(id+"F0.wireOp",EDGE,"E21");var subQ39=sQuery(id+"F0.wireOp",EDGE,"E20");var subQ40=sQuery(id+"F0.wireOp",EDGE,"E19");var subQ41=sQuery(id+"F0.wireOp",EDGE,"E18");var subQ42=sQuery(id+"F0.wireOp",EDGE,"E17");var subQ43=sQuery(id+"F0.wireOp",EDGE,"E16");var subQ44=sQuery(id+"F0.wireOp",EDGE,"E15");var subQ45=sQuery(id+"F0.wireOp",EDGE,"E14");var subQ46=sQuery(id+"F0.wireOp",EDGE,"E13");var subQ47=sQuery(id+"F0.wireOp",EDGE,"E12");var subQ48=sQuery(id+"F0.wireOp",EDGE,"E11");var subQ49=sQuery(id+"F0.wireOp",EDGE,"E10");var subQ50=sQuery(id+"F0.wireOp",EDGE,"E9");var subQ51=sQuery(id+"F0.wireOp",EDGE,"E8");var subQ52=sQuery(id+"F0.wireOp",EDGE,"E7");var subQ53=sQuery(id+"F0.wireOp",EDGE,"E6");var subQ54=sQuery(id+"F0.wireOp",EDGE,"E5");var subQ55=sQuery(id+"F0.wireOp",EDGE,"E4");var subQ56=sQuery(id+"F0.wireOp",EDGE,"E3");var subQ57=sQuery(id+"F0.wireOp",EDGE,"E2");var subQ58=sQuery(id+"F0.wireOp",EDGE,"E1");var subQ59=sQuery(id+"F0.wireOp",EDGE,"E0");Q0=makeQuery(id+"F9.opShell","OFFSET_FACE",FACE,{"disambiguationData":[OSD([subQ59,subQ58,subQ57,subQ56,subQ55,subQ54,subQ53,subQ52,subQ51,subQ50,subQ49,subQ48,subQ47,subQ46,subQ45,subQ44,subQ43,subQ42,subQ41,subQ40,subQ39,subQ38,subQ37,subQ36,subQ35,subQ34,subQ33,subQ32,subQ31,subQ30,subQ29,subQ28,subQ27,subQ26,subQ25,subQ24,subQ23,subQ22,subQ21,subQ20,subQ19,subQ18,subQ17,subQ16,subQ15,subQ14,subQ13,subQ12,subQ11,subQ10,subQ9,subQ8,subQ7,subQ6,subQ5,subQ4,subQ3,subQ2,subQ1,subQ0]),TDD([makeQuery(id+"F1.opExtrude","CAP_FACE",FACE,{"disambiguationData":[OSD([subQ59,subQ58,subQ57,subQ56,subQ55,subQ54,subQ53,subQ52,subQ51,subQ50,subQ49,subQ48,subQ47,subQ46,subQ45,subQ44,subQ43,subQ42,subQ41,subQ40,subQ39,subQ38,subQ37,subQ36,subQ35,subQ34,subQ33,subQ32,subQ31,subQ30,subQ29,subQ28,subQ27,subQ26,subQ25,subQ24,subQ23,subQ22,subQ21,subQ20,subQ19,subQ18,subQ17,subQ16,subQ15,subQ14,subQ13,subQ12,subQ11,subQ10,subQ9,subQ8,subQ7,subQ6,subQ5,subQ4,subQ3,subQ2,subQ1,subQ0])],"isStart":false})]),OD(1.0)]});}
            var sketch = newSketch(context, id + "F10", { "sketchPlane" : qUnion([Q0])});
            skLineSegment(sketch, "E98", {"start": v(21.41, -7.13) * mm, "end": v(31.81, -6.93) * mm});
            skLineSegment(sketch, "E99", {"start": v(20.65, 67.89) * mm, "end": v(29.73, 68.06) * mm});
            skSolve(sketch);
        }
        {
            var Q0;
            {var subQ3=sQuery(id+"F0.wireOp",EDGE,"E1");Q0=makeQuery(id+"F10.imprint","IMPRINT",FACE,{"disambiguationData":[TD([[makeQuery(id+"F10.imprint","IMPRINT",EDGE,{"derivedFrom":makeQuery(id+"F9.opShell","OFFSET_EDGE",EDGE,{"disambiguationData":[OSD([subQ3]),TDD([makeQuery(id+"F1.opExtrude","CAP_EDGE",EDGE,{"disambiguationData":[OSD([subQ3])],"isStart":false})])]})}),1.0]])]});}
            var Q1;
            Q1=makeQuery(id+"F10.imprint","IMPRINT",FACE,{"disambiguationData":[TD([[makeQuery(id+"F10.imprint","IMPRINT",EDGE,{"derivedFrom":sQuery(id+"F10.wireOp",EDGE,"E98")}),-1.0]])]});
            extrude(context, id + "F11", {"entities" : qUnion([Q0, Q1]), "operationType" : NewBodyOperationType.ADD, "endBound" : BoundingType.UP_TO_NEXT, "oppositeDirection" : true, "depth" : 8 * mm, "hasDraft" : true, "draftAngle" : 9 * degree, "draftPullDirection" : true});
        }
        {
            var Q0;
            {var subQ0=sQuery(id+"F0.wireOp",EDGE,"E59.MirrorCS");var subQ1=sQuery(id+"F0.wireOp",EDGE,"E58.MirrorCS");var subQ2=sQuery(id+"F0.wireOp",EDGE,"E30.MirrorCS");var subQ3=sQuery(id+"F0.wireOp",EDGE,"E3");var subQ4=sQuery(id+"F0.wireOp",EDGE,"E2");var subQ5=sQuery(id+"F0.wireOp",EDGE,"E1");var subQ6=sQuery(id+"F0.wireOp",EDGE,"E50.MirrorCS");var subQ7=sQuery(id+"F0.wireOp",EDGE,"E49.MirrorCS");var subQ8=sQuery(id+"F0.wireOp",EDGE,"E48.MirrorCS");var subQ9=sQuery(id+"F0.wireOp",EDGE,"E47.MirrorCS");var subQ10=sQuery(id+"F0.wireOp",EDGE,"E46.MirrorCS");var subQ11=sQuery(id+"F0.wireOp",EDGE,"E45.MirrorCS");var subQ12=sQuery(id+"F0.wireOp",EDGE,"E44.MirrorCS");var subQ13=sQuery(id+"F0.wireOp",EDGE,"E26");var subQ14=sQuery(id+"F0.wireOp",EDGE,"E25");var subQ15=sQuery(id+"F0.wireOp",EDGE,"E24");var subQ16=sQuery(id+"F0.wireOp",EDGE,"E23");var subQ17=sQuery(id+"F0.wireOp",EDGE,"E22");var subQ18=sQuery(id+"F0.wireOp",EDGE,"E21");var subQ19=sQuery(id+"F0.wireOp",EDGE,"E0");var subQ20=sQuery(id+"F0.wireOp",EDGE,"E57.MirrorCS");var subQ21=sQuery(id+"F0.wireOp",EDGE,"E56.MirrorCS");var subQ22=sQuery(id+"F0.wireOp",EDGE,"E55.MirrorCS");var subQ23=sQuery(id+"F0.wireOp",EDGE,"E54.MirrorCS");var subQ24=sQuery(id+"F0.wireOp",EDGE,"E53.MirrorCS");var subQ25=sQuery(id+"F0.wireOp",EDGE,"E52.MirrorCS");var subQ26=sQuery(id+"F0.wireOp",EDGE,"E51.MirrorCS");var subQ27=sQuery(id+"F0.wireOp",EDGE,"E43.MirrorCS");var subQ28=sQuery(id+"F0.wireOp",EDGE,"E42.MirrorCS");var subQ29=sQuery(id+"F0.wireOp",EDGE,"E41.MirrorCS");var subQ30=sQuery(id+"F0.wireOp",EDGE,"E40.MirrorCS");var subQ31=sQuery(id+"F0.wireOp",EDGE,"E39.MirrorCS");var subQ32=sQuery(id+"F0.wireOp",EDGE,"E38.MirrorCS");var subQ33=sQuery(id+"F0.wireOp",EDGE,"E37.MirrorCS");var subQ34=sQuery(id+"F0.wireOp",EDGE,"E36.MirrorCS");var subQ35=sQuery(id+"F0.wireOp",EDGE,"E35.MirrorCS");var subQ36=sQuery(id+"F0.wireOp",EDGE,"E34.MirrorCS");var subQ37=sQuery(id+"F0.wireOp",EDGE,"E33.MirrorCS");var subQ38=sQuery(id+"F0.wireOp",EDGE,"E32.MirrorCS");var subQ39=sQuery(id+"F0.wireOp",EDGE,"E31.MirrorCS");var subQ40=sQuery(id+"F0.wireOp",EDGE,"E29");var subQ41=sQuery(id+"F0.wireOp",EDGE,"E28");var subQ42=sQuery(id+"F0.wireOp",EDGE,"E27");var subQ43=sQuery(id+"F0.wireOp",EDGE,"E20");var subQ44=sQuery(id+"F0.wireOp",EDGE,"E19");var subQ45=sQuery(id+"F0.wireOp",EDGE,"E18");var subQ46=sQuery(id+"F0.wireOp",EDGE,"E17");var subQ47=sQuery(id+"F0.wireOp",EDGE,"E16");var subQ48=sQuery(id+"F0.wireOp",EDGE,"E15");var subQ49=sQuery(id+"F0.wireOp",EDGE,"E14");var subQ50=sQuery(id+"F0.wireOp",EDGE,"E13");var subQ51=sQuery(id+"F0.wireOp",EDGE,"E12");var subQ52=sQuery(id+"F0.wireOp",EDGE,"E11");var subQ53=sQuery(id+"F0.wireOp",EDGE,"E10");var subQ54=sQuery(id+"F0.wireOp",EDGE,"E9");var subQ55=sQuery(id+"F0.wireOp",EDGE,"E8");var subQ56=sQuery(id+"F0.wireOp",EDGE,"E7");var subQ57=sQuery(id+"F0.wireOp",EDGE,"E6");var subQ58=sQuery(id+"F0.wireOp",EDGE,"E5");var subQ59=sQuery(id+"F0.wireOp",EDGE,"E4");Q0=makeQuery(id+"F11.boolean.opBoolean","MERGE",FACE,{"derivedFrom":[makeQuery(id+"F9.opShell","OFFSET_FACE",FACE,{"disambiguationData":[OSD([subQ19,subQ5,subQ4,subQ3,subQ59,subQ58,subQ57,subQ56,subQ55,subQ54,subQ53,subQ52,subQ51,subQ50,subQ49,subQ48,subQ47,subQ46,subQ45,subQ44,subQ43,subQ18,subQ17,subQ16,subQ15,subQ14,subQ13,subQ42,subQ41,subQ40,subQ2,subQ39,subQ38,subQ37,subQ36,subQ35,subQ34,subQ33,subQ32,subQ31,subQ30,subQ29,subQ28,subQ27,subQ12,subQ11,subQ10,subQ9,subQ8,subQ7,subQ6,subQ26,subQ25,subQ24,subQ23,subQ22,subQ21,subQ20,subQ1,subQ0]),TDD([makeQuery(id+"F1.opExtrude","CAP_FACE",FACE,{"disambiguationData":[OSD([subQ19,subQ5,subQ4,subQ3,subQ59,subQ58,subQ57,subQ56,subQ55,subQ54,subQ53,subQ52,subQ51,subQ50,subQ49,subQ48,subQ47,subQ46,subQ45,subQ44,subQ43,subQ18,subQ17,subQ16,subQ15,subQ14,subQ13,subQ42,subQ41,subQ40,subQ2,subQ39,subQ38,subQ37,subQ36,subQ35,subQ34,subQ33,subQ32,subQ31,subQ30,subQ29,subQ28,subQ27,subQ12,subQ11,subQ10,subQ9,subQ8,subQ7,subQ6,subQ26,subQ25,subQ24,subQ23,subQ22,subQ21,subQ20,subQ1,subQ0])],"isStart":false})]),OD(1.0)]}),makeQuery(id+"F11.opExtrude","CAP_FACE",FACE,{"disambiguationData":[OSD([subQ19,subQ18,subQ17,subQ16,subQ15,subQ14,subQ13,subQ12,subQ11,subQ10,subQ9,subQ8,subQ7,subQ6,sQuery(id+"F10.wireOp",EDGE,"E98")])],"isStart":true}),makeQuery(id+"F11.opExtrude","CAP_FACE",FACE,{"disambiguationData":[OSD([subQ5,subQ4,subQ3,subQ2,subQ1,subQ0,sQuery(id+"F10.wireOp",EDGE,"E99")])],"isStart":true})]});}
            var sketch = newSketch(context, id + "F12", { "sketchPlane" : qUnion([Q0])});
            skLineSegment(sketch, "E100", {"start": v(27, -27.83) * mm, "end": v(24.66, 95.99) * mm, "construction": true});
            skCircle(sketch, "E101", {"center": v(25.04, 75.49) * mm, "radius": 2.9 * mm});
            skCircle(sketch, "E102", {"center": v(26.76, -15.03) * mm, "radius": 2.9 * mm});
            skSolve(sketch);
        }
        {
            var Q0;
            Q0=makeQuery(id+"F12.imprint","IMPRINT",FACE,{"disambiguationData":[TD([[makeQuery(id+"F12.imprint","IMPRINT",EDGE,{"derivedFrom":sQuery(id+"F12.wireOp",EDGE,"E101")}),1.0]])]});
            var Q1;
            Q1=makeQuery(id+"F12.imprint","IMPRINT",FACE,{"disambiguationData":[TD([[makeQuery(id+"F12.imprint","IMPRINT",EDGE,{"derivedFrom":sQuery(id+"F12.wireOp",EDGE,"E102")}),1.0]])]});
            extrude(context, id + "F13", {"entities" : qUnion([Q0, Q1]), "operationType" : NewBodyOperationType.REMOVE, "oppositeDirection" : true, "depth" : 6.35 * mm, "offsetDistance" : 25 * mm});
        }
    });
